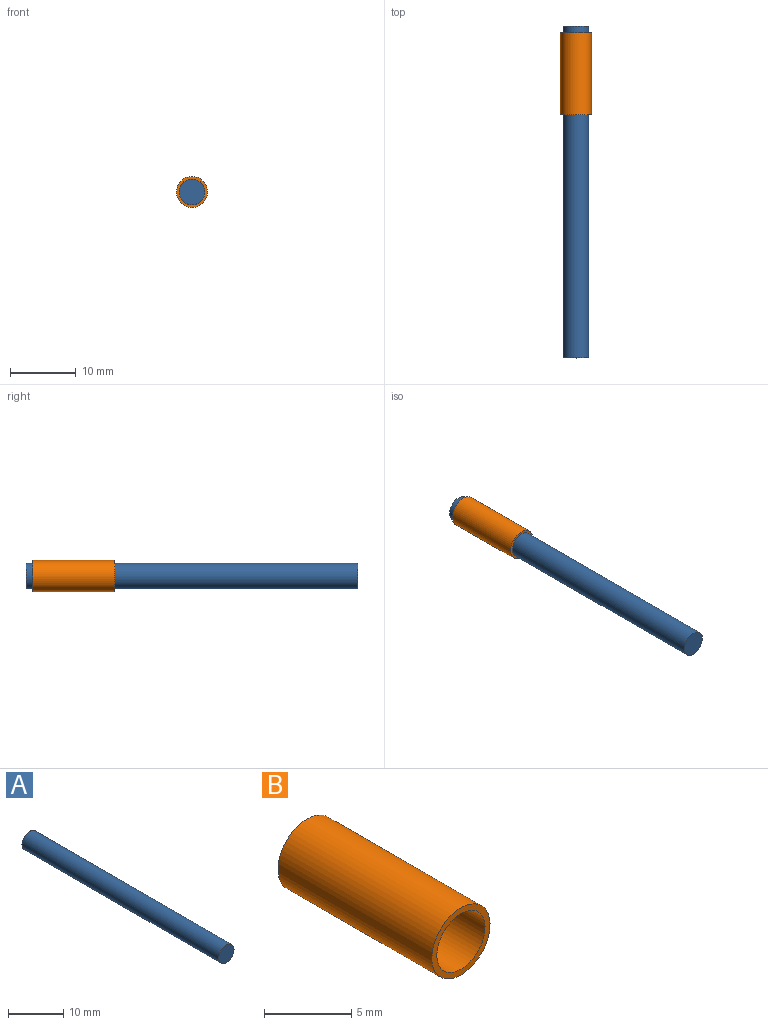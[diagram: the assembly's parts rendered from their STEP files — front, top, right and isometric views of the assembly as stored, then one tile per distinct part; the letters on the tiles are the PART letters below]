
ASSEMBLY  parts=2 mates=1
PART A: 3 faces, bbox 3.9x50.4x3.9 mm
  f0: cylinder r=1.94mm len=50.38mm, axis (0,1,0), area 615.3mm2, adj f1,f2
  f1: plane 3.89x3.89mm, normal (0,-1,0), area 11.9mm2, adj f0
  f2: plane 3.89x3.89mm, normal (0,1,0), area 11.9mm2, adj f0
PART B: 4 faces, bbox 4.7x12.5x4.7 mm
  f0: cylinder r=1.96mm len=12.48mm, axis (0,1,0), area 153.4mm2, adj f2,f3
  f1: cylinder r=2.36mm len=12.48mm, axis (0,1,0), area 185mm2, adj f2,f3
  f2: plane 4.72x4.72mm, normal (0,-1,0), area 5.5mm2, adj f0,f1
  f3: plane 4.72x4.72mm, normal (0,1,0), area 5.5mm2, adj f0,f1
PLACE A t=(13.24,0.08,13.98)mm fixed
PLACE B t=(-6.71,-0.92,17.44)mm
MATE slider A.f0 <-> B.f0  axis (0,1,0) through (-23.86,0.08,64.53)mm
